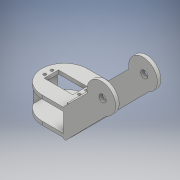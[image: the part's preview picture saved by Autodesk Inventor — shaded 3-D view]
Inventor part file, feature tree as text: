
AUTODESK INVENTOR PART (.ipt)
format: ipt  version: 2018 (Build 220112000, 112)  size: 254,464 bytes
history: native  units: mm
features: extrude x9, sketch x9, other x5, plane x3, mirror x1, fillet x1
ambient origin geometry x8: Origin, YZ Plane, XZ Plane, XY Plane, X Axis, Y Axis, Z Axis, Center Point
bodies: Solid1 (feature_tree)
feature tree (28):
  other  "Femur"
  other  "Blocks"
  plane  "Work Plane10"
  extrude  "Extrusion1"  Depth=2.0mm
  plane  "Work Plane3"
  plane  "Work Plane4"
  mirror  "Mirror3"
  extrude  "Extrusion2"  Depth=10.0mm
  sketch  "Sketch11"  dims[d21=18.5mm d22=37.0mm]
  sketch  "Sketch12"  dims[d23=5.0mm d24=0.0mm d56=5.0mm d57=0.0mm]
  extrude  "Extrusion6"  Depth=37.0mm
  extrude  "Extrusion7"  Depth=5.0mm TaperAngle=0.0deg
  extrude  "Extrusion8"  Depth=21.6mm
  extrude  "Extrusion11"  Depth=5.0mm TaperAngle=0.0deg
  extrude  "Extrusion12"  Depth=10.0mm
  extrude  "Extrusion13"  Depth=5.0mm TaperAngle=0.0deg
  fillet  "Fillet2"  Radius=14.0mm
  extrude  "Extrusion14"  Depth=63.2mm
  sketch  "Sketch4"  dims[d4=20.0mm d5=2.0mm]
  sketch  "Sketch9"  dims[d7=5.0mm d8=0.0mm d20=10.0mm]
  sketch  "Sketch18"  dims[d61=57.0mm d62=0.0mm d73=21.6mm]
  sketch  "Sketch21"  dims[d74=1.100149mm d75=5.0mm d76=0.0mm]
  other  "servo_frontal"
  other  "servo_con_eje"
  sketch  "Sketch28"  dims[d85=10.0mm d86=31.598344mm]
  sketch  "Sketch29"  dims[d87=6.0mm d88=0.0mm d90=5.0mm d91=0.0mm d92=14.0mm]
  sketch  "Sketch31"  dims[d93=63.2mm d94=63.2mm d95=63.2mm d96=5.0mm d97=5.0mm d98=63.2mm d99=5.0mm d100=0.0mm d101=32.0mm d103=5.0mm d104=0.0mm]
  other  "servo_frontal:1"
